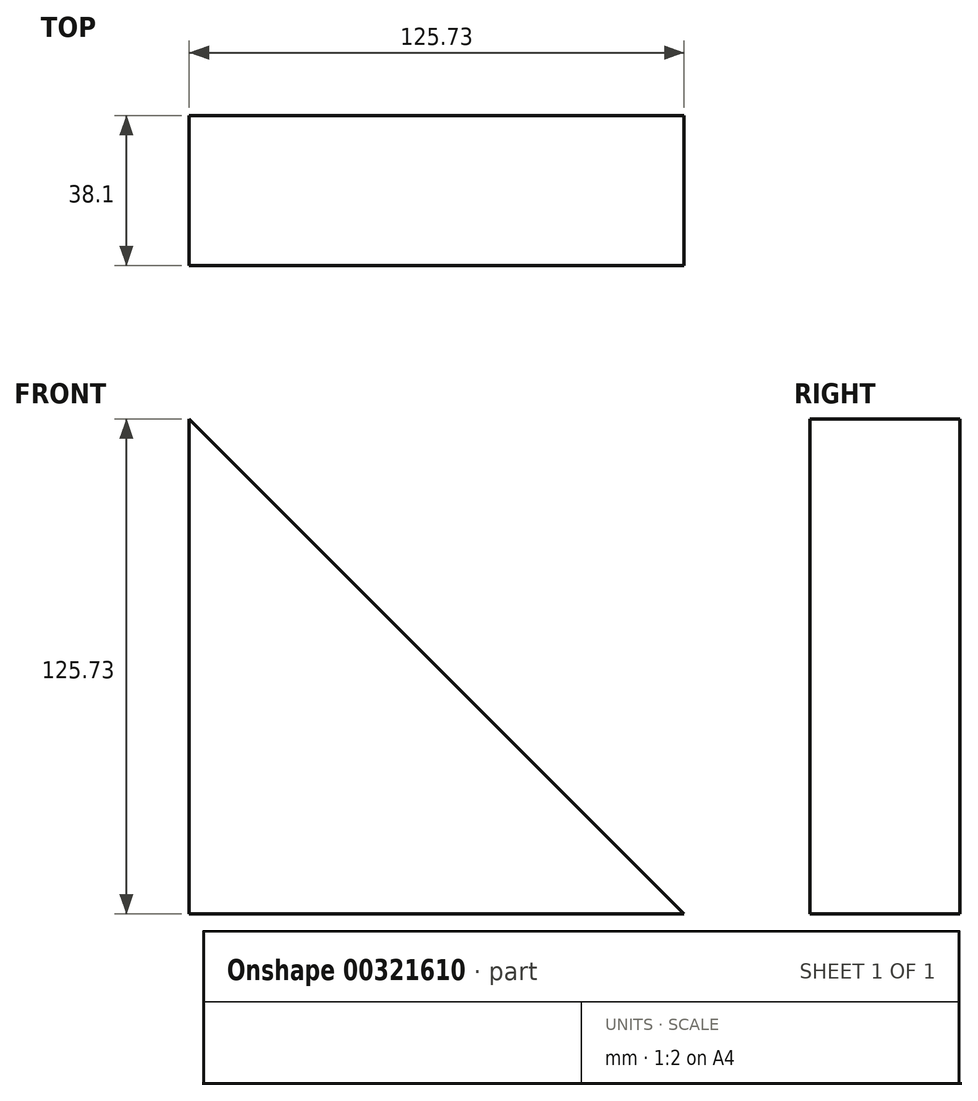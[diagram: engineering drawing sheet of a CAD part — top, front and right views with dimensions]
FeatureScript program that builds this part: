
annotation { "Feature Type Name" : "Feature", "Feature Type Description" : "" }
export const myFeature = defineFeature(function(context is Context, id is Id, definition is map)
    precondition{}
    {
        {
            var Q0;
            Q0=qCreatedBy(makeId("Front.planeOp"),FACE);
            var sketch = newSketch(context, id + "F0", { "sketchPlane" : qUnion([Q0])});
            skLineSegment(sketch, "E0", {"start": v(0, 0) * mm, "end": v(0, 125.73) * mm});
            skLineSegment(sketch, "E1", {"start": v(0, 125.73) * mm, "end": v(125.73, 0) * mm});
            skLineSegment(sketch, "E2", {"start": v(125.73, 0) * mm, "end": v(0, 0) * mm});
            skSolve(sketch);
        }
        {
            var Q0;
            Q0=makeQuery(id+"F0.imprint","IMPRINT",FACE,{"disambiguationData":[TD([[makeQuery(id+"F0.imprint","IMPRINT",EDGE,{"derivedFrom":sQuery(id+"F0.wireOp",EDGE,"E0")}),-1.0]])]});
            extrude(context, id + "F1", {"entities" : qUnion([Q0]), "depth" : 38.1 * mm});
        }
    });
